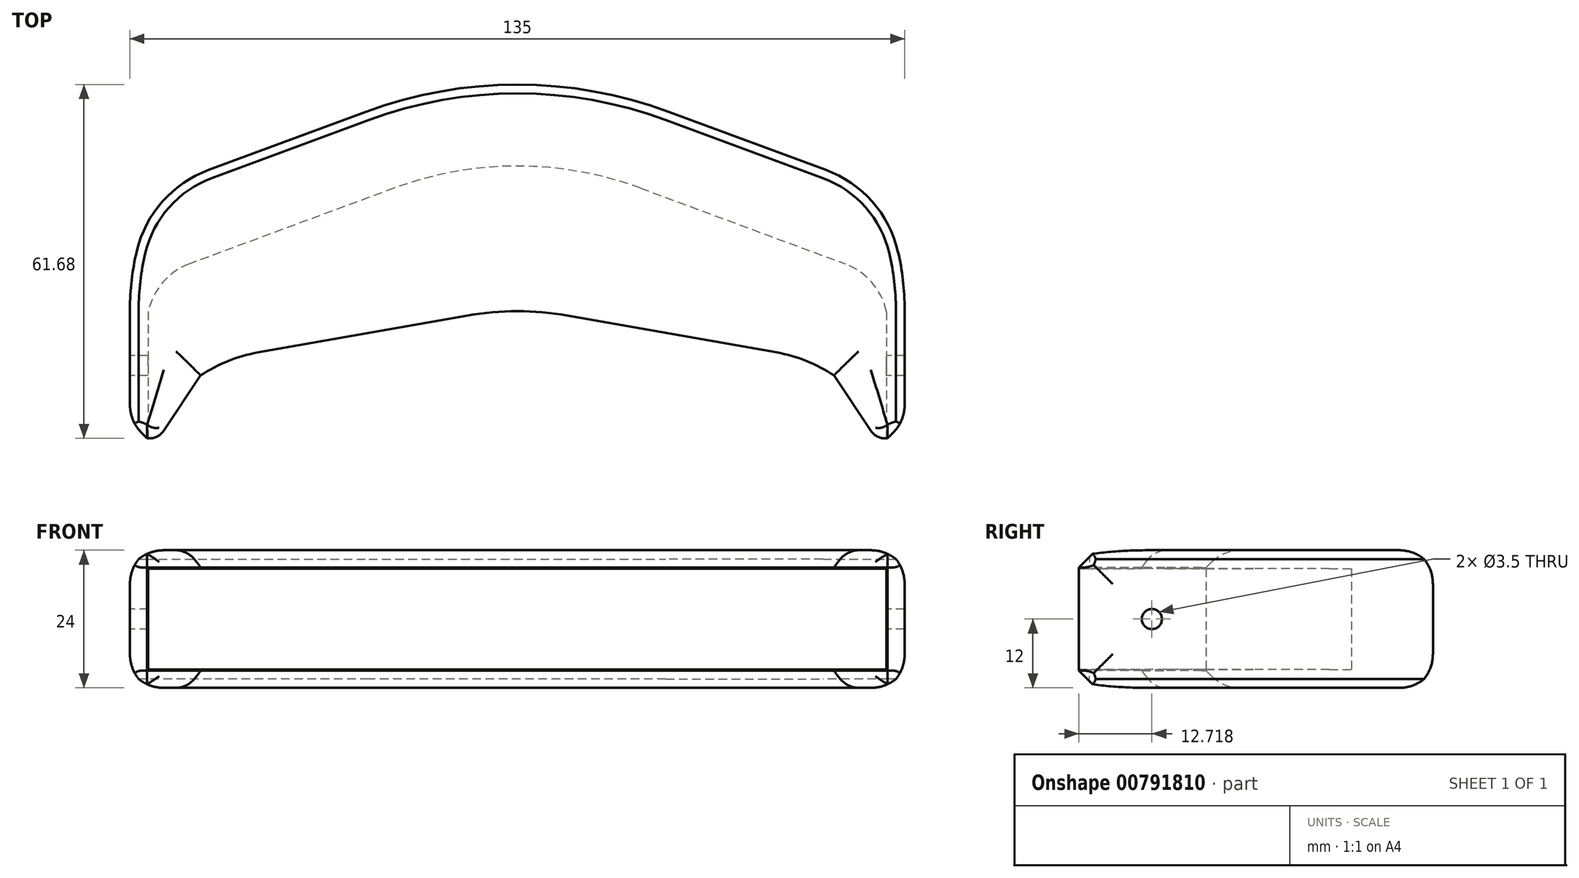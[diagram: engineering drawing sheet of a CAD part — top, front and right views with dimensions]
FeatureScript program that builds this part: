
annotation { "Feature Type Name" : "Feature", "Feature Type Description" : "" }
export const myFeature = defineFeature(function(context is Context, id is Id, definition is map)
    precondition{}
    {
        {
            var Q0;
            Q0=qCreatedBy(makeId("Top.planeOp"),FACE);
            var sketch = newSketch(context, id + "F0", { "sketchPlane" : qUnion([Q0])});
            skLineSegment(sketch, "E0.left", {"start": v(-67.5, -4.63) * mm, "end": v(-67.5, -27.07) * mm});
            skLineSegment(sketch, "E0.right", {"start": v(67.5, -4.63) * mm, "end": v(67.5, -27.07) * mm});
            skLineSegment(sketch, "E1", {"start": v(-22.58, 19.56) * mm, "end": v(-58.22, 6.36) * mm});
            skLineSegment(sketch, "E2", {"start": v(22.58, 19.56) * mm, "end": v(58.25, 6.35) * mm});
            skPoint(sketch, "E3.visualSharp", {"position": v(-67.5, 2.93) * mm});
            skPoint(sketch, "E4.visualSharp", {"position": v(67.5, 2.93) * mm});
            skPoint(sketch, "E5.visualSharp", {"position": v(0, 27.93) * mm});
            skArc(sketch, "E5.filletArc", {"start": v(22.58, 19.56) * mm, "mid": v(0, 23.61) * mm, "end": v(-22.58, 19.56) * mm});
            skLineSegment(sketch, "E6", {"start": v(-67.5, -27.07) * mm, "end": v(-64.1, -27.07) * mm});
            skLineSegment(sketch, "E7", {"start": v(-61.6, -25.74) * mm, "end": v(-55.17, -16.09) * mm});
            skLineSegment(sketch, "E8", {"start": v(67.5, -27.07) * mm, "end": v(64.1, -27.07) * mm});
            skLineSegment(sketch, "E9", {"start": v(61.6, -25.74) * mm, "end": v(55.17, -16.09) * mm});
            skPoint(sketch, "E10.visualSharp", {"position": v(-52.5, -12.08) * mm});
            skPoint(sketch, "E11.visualSharp", {"position": v(52.5, -12.08) * mm});
            skPoint(sketch, "E12.visualSharp", {"position": v(62.5, -27.07) * mm});
            skArc(sketch, "E12.filletArc", {"start": v(61.6, -25.74) * mm, "mid": v(62.69, -26.72) * mm, "end": v(64.1, -27.07) * mm});
            skPoint(sketch, "E13.visualSharp", {"position": v(-62.5, -27.07) * mm});
            skArc(sketch, "E13.filletArc", {"start": v(-64.1, -27.07) * mm, "mid": v(-62.69, -26.72) * mm, "end": v(-61.6, -25.74) * mm});
            skLineSegment(sketch, "E14", {"start": v(-45.18, -12.08) * mm, "end": v(-8.66, -5.66) * mm});
            skLineSegment(sketch, "E15", {"start": v(8.66, -5.66) * mm, "end": v(45.18, -12.08) * mm});
            skPoint(sketch, "E16.visualSharp", {"position": v(0, -4.13) * mm});
            skArc(sketch, "E16.filletArc", {"start": v(8.66, -5.66) * mm, "mid": v(0, -4.9) * mm, "end": v(-8.66, -5.66) * mm});
            skPoint(sketch, "E17.visualSharp", {"position": v(-63.32, 13.1) * mm});
            skPoint(sketch, "E18.visualSharp", {"position": v(58.32, 13.1) * mm});
            skArc(sketch, "E19", {"start": v(-58.22, 6.36) * mm, "mid": v(-64.3, 2.09) * mm, "end": v(-67.5, -4.63) * mm});
            skArc(sketch, "E20", {"start": v(67.5, -4.63) * mm, "mid": v(64.32, 2.08) * mm, "end": v(58.25, 6.35) * mm});
            skArc(sketch, "E21", {"start": v(-45.18, -12.08) * mm, "mid": v(-50.39, -13.57) * mm, "end": v(-55.17, -16.09) * mm});
            skArc(sketch, "E22", {"start": v(55.17, -16.09) * mm, "mid": v(50.39, -13.57) * mm, "end": v(45.18, -12.08) * mm});
            skPoint(sketch, "E23.visualSharp", {"position": v(-61, 13.86) * mm});
            skPoint(sketch, "E24.visualSharp", {"position": v(61.03, 13.85) * mm});
            skSolve(sketch);
        }
        {
            var Q0;
            Q0=qSketchRegion(id+"F0",true);
            extrude(context, id + "F1", {"entities" : qUnion([Q0]), "depth" : 24 * mm, "offsetDistance" : 25 * mm});
        }
        {
            var Q0;
            Q0=makeQuery(id+"F1.opExtrude","SWEPT_FACE",FACE,{"disambiguationData":[OSD([sQuery(id+"F0.wireOp",EDGE,"E14")])]});
            var Q1;
            Q1=makeQuery(id+"F1.opExtrude","SWEPT_FACE",FACE,{"disambiguationData":[OSD([sQuery(id+"F0.wireOp",EDGE,"E16.filletArc")])]});
            var Q2;
            Q2=makeQuery(id+"F1.opExtrude","SWEPT_FACE",FACE,{"disambiguationData":[OSD([sQuery(id+"F0.wireOp",EDGE,"E15")])]});
            var Q3;
            Q3=makeQuery(id+"F1.opExtrude","SWEPT_FACE",FACE,{"disambiguationData":[OSD([sQuery(id+"F0.wireOp",EDGE,"E11.filletArc")])]});
            var Q4;
            Q4=makeQuery(id+"F1.opExtrude","SWEPT_FACE",FACE,{"disambiguationData":[OSD([sQuery(id+"F0.wireOp",EDGE,"E9")])]});
            var Q5;
            Q5=makeQuery(id+"F1.opExtrude","SWEPT_FACE",FACE,{"disambiguationData":[OSD([sQuery(id+"F0.wireOp",EDGE,"E12.filletArc")])]});
            var Q6;
            Q6=makeQuery(id+"F1.opExtrude","SWEPT_FACE",FACE,{"disambiguationData":[OSD([sQuery(id+"F0.wireOp",EDGE,"E7")])]});
            var Q7;
            Q7=makeQuery(id+"F1.opExtrude","SWEPT_FACE",FACE,{"disambiguationData":[OSD([sQuery(id+"F0.wireOp",EDGE,"E10.filletArc")])]});
            var Q8;
            Q8=makeQuery(id+"F1.opExtrude","SWEPT_FACE",FACE,{"disambiguationData":[OSD([sQuery(id+"F0.wireOp",EDGE,"E13.filletArc")])]});
            var Q9;
            Q9=makeQuery(id+"F1.opExtrude","SWEPT_FACE",FACE,{"disambiguationData":[OSD([sQuery(id+"F0.wireOp",EDGE,"E6")])]});
            var Q10;
            Q10=makeQuery(id+"F1.opExtrude","SWEPT_FACE",FACE,{"disambiguationData":[OSD([sQuery(id+"F0.wireOp",EDGE,"E8")])]});
            var Q11;
            Q11=makeQuery(id+"F1.opExtrude","SWEPT_FACE",FACE,{"disambiguationData":[OSD([sQuery(id+"F0.wireOp",EDGE,"E21")])]});
            var Q12;
            Q12=makeQuery(id+"F1.opExtrude","SWEPT_FACE",FACE,{"disambiguationData":[OSD([sQuery(id+"F0.wireOp",EDGE,"E22")])]});
            shell(context, id + "F2", {"entities" : qUnion([Q0, Q1, Q2, Q3, Q4, Q5, Q6, Q7, Q8, Q9, Q10, Q11, Q12]), "thickness" : 3.2 * mm});
        }
        {
            var Q0;
            Q0=makeQuery(id+"F1.opExtrude","CAP_FACE",FACE,{"disambiguationData":[OSD([sQuery(id+"F0.wireOp",EDGE,"E0.left"),sQuery(id+"F0.wireOp",EDGE,"E0.right"),sQuery(id+"F0.wireOp",EDGE,"E1"),sQuery(id+"F0.wireOp",EDGE,"E2"),sQuery(id+"F0.wireOp",EDGE,"E3.filletArc"),sQuery(id+"F0.wireOp",EDGE,"E4.filletArc"),sQuery(id+"F0.wireOp",EDGE,"E5.filletArc"),sQuery(id+"F0.wireOp",EDGE,"E6"),sQuery(id+"F0.wireOp",EDGE,"E7"),sQuery(id+"F0.wireOp",EDGE,"E8"),sQuery(id+"F0.wireOp",EDGE,"E9"),sQuery(id+"F0.wireOp",EDGE,"E10.filletArc"),sQuery(id+"F0.wireOp",EDGE,"E11.filletArc"),sQuery(id+"F0.wireOp",EDGE,"E12.filletArc"),sQuery(id+"F0.wireOp",EDGE,"E13.filletArc"),sQuery(id+"F0.wireOp",EDGE,"E14"),sQuery(id+"F0.wireOp",EDGE,"E15"),sQuery(id+"F0.wireOp",EDGE,"E16.filletArc")])],"isStart":false});
            var sketch = newSketch(context, id + "F3", { "sketchPlane" : qUnion([Q0])});
            skLineSegment(sketch, "E25", {"start": v(-22.58, 19.56) * mm, "end": v(-58.22, 6.36) * mm});
            skLineSegment(sketch, "E26", {"start": v(22.58, 19.56) * mm, "end": v(58.25, 6.35) * mm});
            skArc(sketch, "E27.filletArc", {"start": v(22.58, 19.56) * mm, "mid": v(0, 23.61) * mm, "end": v(-22.58, 19.56) * mm});
            skArc(sketch, "E28", {"start": v(-58.22, 6.36) * mm, "mid": v(-64.3, 2.09) * mm, "end": v(-67.5, -4.63) * mm});
            skArc(sketch, "E29", {"start": v(67.5, -4.63) * mm, "mid": v(64.32, 2.08) * mm, "end": v(58.25, 6.35) * mm});
            skLineSegment(sketch, "E30.0", {"start": v(-26.4, 29.88) * mm, "end": v(-53.8, 19.73) * mm});
            skArc(sketch, "E30.1", {"start": v(26.4, 29.88) * mm, "mid": v(0, 34.61) * mm, "end": v(-26.4, 29.88) * mm});
            skLineSegment(sketch, "E30.2", {"start": v(26.4, 29.88) * mm, "end": v(53.8, 19.73) * mm});
            skArc(sketch, "E31", {"start": v(-66.3, 5.59) * mm, "mid": v(-67.2, 0.51) * mm, "end": v(-67.5, -4.63) * mm});
            skArc(sketch, "E32", {"start": v(67.5, -4.63) * mm, "mid": v(67.2, 0.5) * mm, "end": v(66.32, 5.56) * mm});
            skPoint(sketch, "E33.visualSharp", {"position": v(-62.04, 16.68) * mm});
            skArc(sketch, "E33.filletArc", {"start": v(-53.8, 19.73) * mm, "mid": v(-61.82, 14.23) * mm, "end": v(-66.3, 5.59) * mm});
            skPoint(sketch, "E34.visualSharp", {"position": v(62.07, 16.67) * mm});
            skArc(sketch, "E34.filletArc", {"start": v(66.32, 5.56) * mm, "mid": v(61.84, 14.22) * mm, "end": v(53.8, 19.73) * mm});
            skSolve(sketch);
        }
        {
            var Q0;
            Q0=qSketchRegion(id+"F3",true);
            extrude(context, id + "F4", {"entities" : qUnion([Q0]), "operationType" : NewBodyOperationType.ADD, "oppositeDirection" : true, "depth" : 24 * mm, "offsetDistance" : 25 * mm});
        }
        {
            var Q0;
            Q0=makeQuery(id+"F4.boolean.opBoolean","MERGE",FACE,{"derivedFrom":[makeQuery(id+"F1.opExtrude","CAP_FACE",FACE,{"disambiguationData":[OSD([sQuery(id+"F0.wireOp",EDGE,"E0.left"),sQuery(id+"F0.wireOp",EDGE,"E0.right"),sQuery(id+"F0.wireOp",EDGE,"E1"),sQuery(id+"F0.wireOp",EDGE,"E2"),sQuery(id+"F0.wireOp",EDGE,"E3.filletArc"),sQuery(id+"F0.wireOp",EDGE,"E4.filletArc"),sQuery(id+"F0.wireOp",EDGE,"E5.filletArc"),sQuery(id+"F0.wireOp",EDGE,"E6"),sQuery(id+"F0.wireOp",EDGE,"E7"),sQuery(id+"F0.wireOp",EDGE,"E8"),sQuery(id+"F0.wireOp",EDGE,"E9"),sQuery(id+"F0.wireOp",EDGE,"E10.filletArc"),sQuery(id+"F0.wireOp",EDGE,"E11.filletArc"),sQuery(id+"F0.wireOp",EDGE,"E12.filletArc"),sQuery(id+"F0.wireOp",EDGE,"E13.filletArc"),sQuery(id+"F0.wireOp",EDGE,"E14"),sQuery(id+"F0.wireOp",EDGE,"E15"),sQuery(id+"F0.wireOp",EDGE,"E16.filletArc")])],"isStart":false}),makeQuery(id+"F4.opExtrude","CAP_FACE",FACE,{"disambiguationData":[OSD([sQuery(id+"F3.wireOp",EDGE,"276efb32-5cb6-4f63-bdc1-496fc01c60db.2"),sQuery(id+"F3.wireOp",EDGE,"276efb32-5cb6-4f63-bdc1-496fc01c60db.3"),sQuery(id+"F3.wireOp",EDGE,"276efb32-5cb6-4f63-bdc1-496fc01c60db.4"),sQuery(id+"F3.wireOp",EDGE,"0241c868-49d8-4b9a-ac46-58dfbb5efc39"),sQuery(id+"F3.wireOp",EDGE,"348bde47-0a47-42e3-8267-499f4a5522ae"),sQuery(id+"F3.wireOp",EDGE,"215ec280-f68a-4f47-a865-032d440a2936.filletArc"),sQuery(id+"F3.wireOp",EDGE,"fd759fa0-5ab4-4b6e-8cb0-b494d0b887aa.filletArc"),sQuery(id+"F3.wireOp",EDGE,"73b2d2fd-a5d6-4b7d-9539-ec2af92cbbd5"),sQuery(id+"F3.wireOp",EDGE,"2c1b0ead-8098-4b90-8860-aa6a1cb84409"),sQuery(id+"F3.wireOp",EDGE,"515ed680-fa81-4fbc-94c5-9d26c9a30982.filletArc"),sQuery(id+"F3.wireOp",EDGE,"67b69344-5ccb-49e4-9dbe-6815e7e981bc.filletArc"),sQuery(id+"F3.wireOp",EDGE,"a765c2de-9442-403f-932b-7ea1a12a6cac.filletArc")])],"isStart":true})]});
            var Q1;
            Q1=makeQuery(id+"F4.boolean.opBoolean","MERGE",FACE,{"derivedFrom":[makeQuery(id+"F1.opExtrude","CAP_FACE",FACE,{"disambiguationData":[OSD([sQuery(id+"F0.wireOp",EDGE,"E0.left"),sQuery(id+"F0.wireOp",EDGE,"E0.right"),sQuery(id+"F0.wireOp",EDGE,"E1"),sQuery(id+"F0.wireOp",EDGE,"E2"),sQuery(id+"F0.wireOp",EDGE,"E3.filletArc"),sQuery(id+"F0.wireOp",EDGE,"E4.filletArc"),sQuery(id+"F0.wireOp",EDGE,"E5.filletArc"),sQuery(id+"F0.wireOp",EDGE,"E6"),sQuery(id+"F0.wireOp",EDGE,"E7"),sQuery(id+"F0.wireOp",EDGE,"E8"),sQuery(id+"F0.wireOp",EDGE,"E9"),sQuery(id+"F0.wireOp",EDGE,"E10.filletArc"),sQuery(id+"F0.wireOp",EDGE,"E11.filletArc"),sQuery(id+"F0.wireOp",EDGE,"E12.filletArc"),sQuery(id+"F0.wireOp",EDGE,"E13.filletArc"),sQuery(id+"F0.wireOp",EDGE,"E14"),sQuery(id+"F0.wireOp",EDGE,"E15"),sQuery(id+"F0.wireOp",EDGE,"E16.filletArc")])],"isStart":true}),makeQuery(id+"F4.opExtrude","CAP_FACE",FACE,{"disambiguationData":[OSD([sQuery(id+"F3.wireOp",EDGE,"276efb32-5cb6-4f63-bdc1-496fc01c60db.2"),sQuery(id+"F3.wireOp",EDGE,"276efb32-5cb6-4f63-bdc1-496fc01c60db.3"),sQuery(id+"F3.wireOp",EDGE,"276efb32-5cb6-4f63-bdc1-496fc01c60db.4"),sQuery(id+"F3.wireOp",EDGE,"0241c868-49d8-4b9a-ac46-58dfbb5efc39"),sQuery(id+"F3.wireOp",EDGE,"348bde47-0a47-42e3-8267-499f4a5522ae"),sQuery(id+"F3.wireOp",EDGE,"215ec280-f68a-4f47-a865-032d440a2936.filletArc"),sQuery(id+"F3.wireOp",EDGE,"fd759fa0-5ab4-4b6e-8cb0-b494d0b887aa.filletArc"),sQuery(id+"F3.wireOp",EDGE,"73b2d2fd-a5d6-4b7d-9539-ec2af92cbbd5"),sQuery(id+"F3.wireOp",EDGE,"2c1b0ead-8098-4b90-8860-aa6a1cb84409"),sQuery(id+"F3.wireOp",EDGE,"515ed680-fa81-4fbc-94c5-9d26c9a30982.filletArc"),sQuery(id+"F3.wireOp",EDGE,"67b69344-5ccb-49e4-9dbe-6815e7e981bc.filletArc"),sQuery(id+"F3.wireOp",EDGE,"a765c2de-9442-403f-932b-7ea1a12a6cac.filletArc")])],"isStart":false})]});
            var Q2;
            Q2=makeQuery(id+"F1.opExtrude","SWEPT_EDGE",EDGE,{"disambiguationData":[OSD([sQuery(id+"F0.wireOp",EDGE,"E0.left"),sQuery(id+"F0.wireOp",EDGE,"E6")])]});
            var Q3;
            Q3=makeQuery(id+"F1.opExtrude","SWEPT_EDGE",EDGE,{"disambiguationData":[OSD([sQuery(id+"F0.wireOp",EDGE,"E0.right"),sQuery(id+"F0.wireOp",EDGE,"E8")])]});
            chamfer(context, id + "F5", {"entities" : qUnion([Q0, Q1, Q2, Q3]), "width" : 3 * mm, "tangentPropagation" : true});
        }
        {
            var Q0;
            Q0=makeQuery(id+"F1.opExtrude","SWEPT_FACE",FACE,{"disambiguationData":[OSD([sQuery(id+"F0.wireOp",EDGE,"E0.left")])]});
            var sketch = newSketch(context, id + "F6", { "sketchPlane" : qUnion([Q0])});
            skCircle(sketch, "E35", {"center": v(14.35, 12) * mm, "radius": 1.75 * mm});
            skPoint(sketch, "E36", {"position": v(24.07, 12) * mm});
            skPoint(sketch, "E37", {"position": v(14.35, 21) * mm});
            skSolve(sketch);
        }
        {
            var Q0;
            Q0=qSketchRegion(id+"F6",true);
            extrude(context, id + "F7", {"entities" : qUnion([Q0]), "operationType" : NewBodyOperationType.REMOVE, "oppositeDirection" : true, "depth" : 140 * mm, "offsetDistance" : 25 * mm});
        }
        {
            var Q0;
            Q0=makeQuery(id+"F4.boolean.opBoolean","MERGE",FACE,{"derivedFrom":[makeQuery(id+"F1.opExtrude","CAP_FACE",FACE,{"disambiguationData":[OSD([sQuery(id+"F0.wireOp",EDGE,"E0.left"),sQuery(id+"F0.wireOp",EDGE,"E0.right"),sQuery(id+"F0.wireOp",EDGE,"E1"),sQuery(id+"F0.wireOp",EDGE,"E2"),sQuery(id+"F0.wireOp",EDGE,"E5.filletArc"),sQuery(id+"F0.wireOp",EDGE,"E6"),sQuery(id+"F0.wireOp",EDGE,"E7"),sQuery(id+"F0.wireOp",EDGE,"E8"),sQuery(id+"F0.wireOp",EDGE,"E9"),sQuery(id+"F0.wireOp",EDGE,"E12.filletArc"),sQuery(id+"F0.wireOp",EDGE,"E13.filletArc"),sQuery(id+"F0.wireOp",EDGE,"E14"),sQuery(id+"F0.wireOp",EDGE,"E15"),sQuery(id+"F0.wireOp",EDGE,"E16.filletArc"),sQuery(id+"F0.wireOp",EDGE,"E19"),sQuery(id+"F0.wireOp",EDGE,"E20"),sQuery(id+"F0.wireOp",EDGE,"E21"),sQuery(id+"F0.wireOp",EDGE,"E22")])],"isStart":false}),makeQuery(id+"F4.opExtrude","CAP_FACE",FACE,{"disambiguationData":[OSD([sQuery(id+"F3.wireOp",EDGE,"E25"),sQuery(id+"F3.wireOp",EDGE,"E26"),sQuery(id+"F3.wireOp",EDGE,"E27.filletArc"),sQuery(id+"F3.wireOp",EDGE,"E28"),sQuery(id+"F3.wireOp",EDGE,"E29"),sQuery(id+"F3.wireOp",EDGE,"E30.0"),sQuery(id+"F3.wireOp",EDGE,"E30.1"),sQuery(id+"F3.wireOp",EDGE,"E30.2"),sQuery(id+"F3.wireOp",EDGE,"E31"),sQuery(id+"F3.wireOp",EDGE,"E32"),sQuery(id+"F3.wireOp",EDGE,"E33.filletArc"),sQuery(id+"F3.wireOp",EDGE,"E34.filletArc")])],"isStart":true})]});
            var Q1;
            Q1=makeQuery(id+"F4.boolean.opBoolean","MERGE",FACE,{"derivedFrom":[makeQuery(id+"F1.opExtrude","CAP_FACE",FACE,{"disambiguationData":[OSD([sQuery(id+"F0.wireOp",EDGE,"E0.left"),sQuery(id+"F0.wireOp",EDGE,"E0.right"),sQuery(id+"F0.wireOp",EDGE,"E1"),sQuery(id+"F0.wireOp",EDGE,"E2"),sQuery(id+"F0.wireOp",EDGE,"E5.filletArc"),sQuery(id+"F0.wireOp",EDGE,"E6"),sQuery(id+"F0.wireOp",EDGE,"E7"),sQuery(id+"F0.wireOp",EDGE,"E8"),sQuery(id+"F0.wireOp",EDGE,"E9"),sQuery(id+"F0.wireOp",EDGE,"E12.filletArc"),sQuery(id+"F0.wireOp",EDGE,"E13.filletArc"),sQuery(id+"F0.wireOp",EDGE,"E14"),sQuery(id+"F0.wireOp",EDGE,"E15"),sQuery(id+"F0.wireOp",EDGE,"E16.filletArc"),sQuery(id+"F0.wireOp",EDGE,"E19"),sQuery(id+"F0.wireOp",EDGE,"E20"),sQuery(id+"F0.wireOp",EDGE,"E21"),sQuery(id+"F0.wireOp",EDGE,"E22")])],"isStart":true}),makeQuery(id+"F4.opExtrude","CAP_FACE",FACE,{"disambiguationData":[OSD([sQuery(id+"F3.wireOp",EDGE,"E25"),sQuery(id+"F3.wireOp",EDGE,"E26"),sQuery(id+"F3.wireOp",EDGE,"E27.filletArc"),sQuery(id+"F3.wireOp",EDGE,"E28"),sQuery(id+"F3.wireOp",EDGE,"E29"),sQuery(id+"F3.wireOp",EDGE,"E30.0"),sQuery(id+"F3.wireOp",EDGE,"E30.1"),sQuery(id+"F3.wireOp",EDGE,"E30.2"),sQuery(id+"F3.wireOp",EDGE,"E31"),sQuery(id+"F3.wireOp",EDGE,"E32"),sQuery(id+"F3.wireOp",EDGE,"E33.filletArc"),sQuery(id+"F3.wireOp",EDGE,"E34.filletArc")])],"isStart":false})]});
            var Q2;
            {var subQ0=sQuery(id+"F0.wireOp",EDGE,"E0.left");Q2=makeQuery(id+"F5.opChamfer","BLEND_EDGE",EDGE,{"blendedFrom":[makeQuery(id+"F1.opExtrude","CAP_EDGE",EDGE,{"disambiguationData":[OSD([subQ0])],"isStart":false}),makeQuery(id+"F1.opExtrude","SWEPT_FACE",FACE,{"disambiguationData":[OSD([subQ0])]})],"blendedInto":[makeQuery(id+"F1.opExtrude","SWEPT_FACE",FACE,{"disambiguationData":[OSD([subQ0])]})]});}
            var Q3;
            {var subQ0=sQuery(id+"F0.wireOp",EDGE,"E0.left");Q3=makeQuery(id+"F5.opChamfer","BLEND_EDGE",EDGE,{"blendedFrom":[makeQuery(id+"F1.opExtrude","CAP_EDGE",EDGE,{"disambiguationData":[OSD([subQ0])],"isStart":true}),makeQuery(id+"F1.opExtrude","SWEPT_FACE",FACE,{"disambiguationData":[OSD([subQ0])]})],"blendedInto":[makeQuery(id+"F1.opExtrude","SWEPT_FACE",FACE,{"disambiguationData":[OSD([subQ0])]})]});}
            var Q4;
            {var subQ0=sQuery(id+"F0.wireOp",EDGE,"E0.right");Q4=makeQuery(id+"F5.opChamfer","BLEND_EDGE",EDGE,{"blendedFrom":[makeQuery(id+"F1.opExtrude","SWEPT_EDGE",EDGE,{"disambiguationData":[OSD([subQ0,sQuery(id+"F0.wireOp",EDGE,"E8")])]}),makeQuery(id+"F1.opExtrude","SWEPT_FACE",FACE,{"disambiguationData":[OSD([subQ0])]})],"blendedInto":[makeQuery(id+"F1.opExtrude","SWEPT_FACE",FACE,{"disambiguationData":[OSD([subQ0])]})]});}
            var Q5;
            {var subQ0=sQuery(id+"F0.wireOp",EDGE,"E0.left");Q5=makeQuery(id+"F5.opChamfer","BLEND_EDGE",EDGE,{"blendedFrom":[makeQuery(id+"F1.opExtrude","SWEPT_EDGE",EDGE,{"disambiguationData":[OSD([subQ0,sQuery(id+"F0.wireOp",EDGE,"E6")])]}),makeQuery(id+"F1.opExtrude","SWEPT_FACE",FACE,{"disambiguationData":[OSD([subQ0])]})],"blendedInto":[makeQuery(id+"F1.opExtrude","SWEPT_FACE",FACE,{"disambiguationData":[OSD([subQ0])]})]});}
            fillet(context, id + "F8", {"entities" : qUnion([Q0, Q1, Q2, Q3, Q4, Q5]), "tangentPropagation" : true, "radius" : 7 * mm, "defaultsChanged" : false, "vertexSettings" : [], "allowEdgeOverflow" : false});
        }
    });
